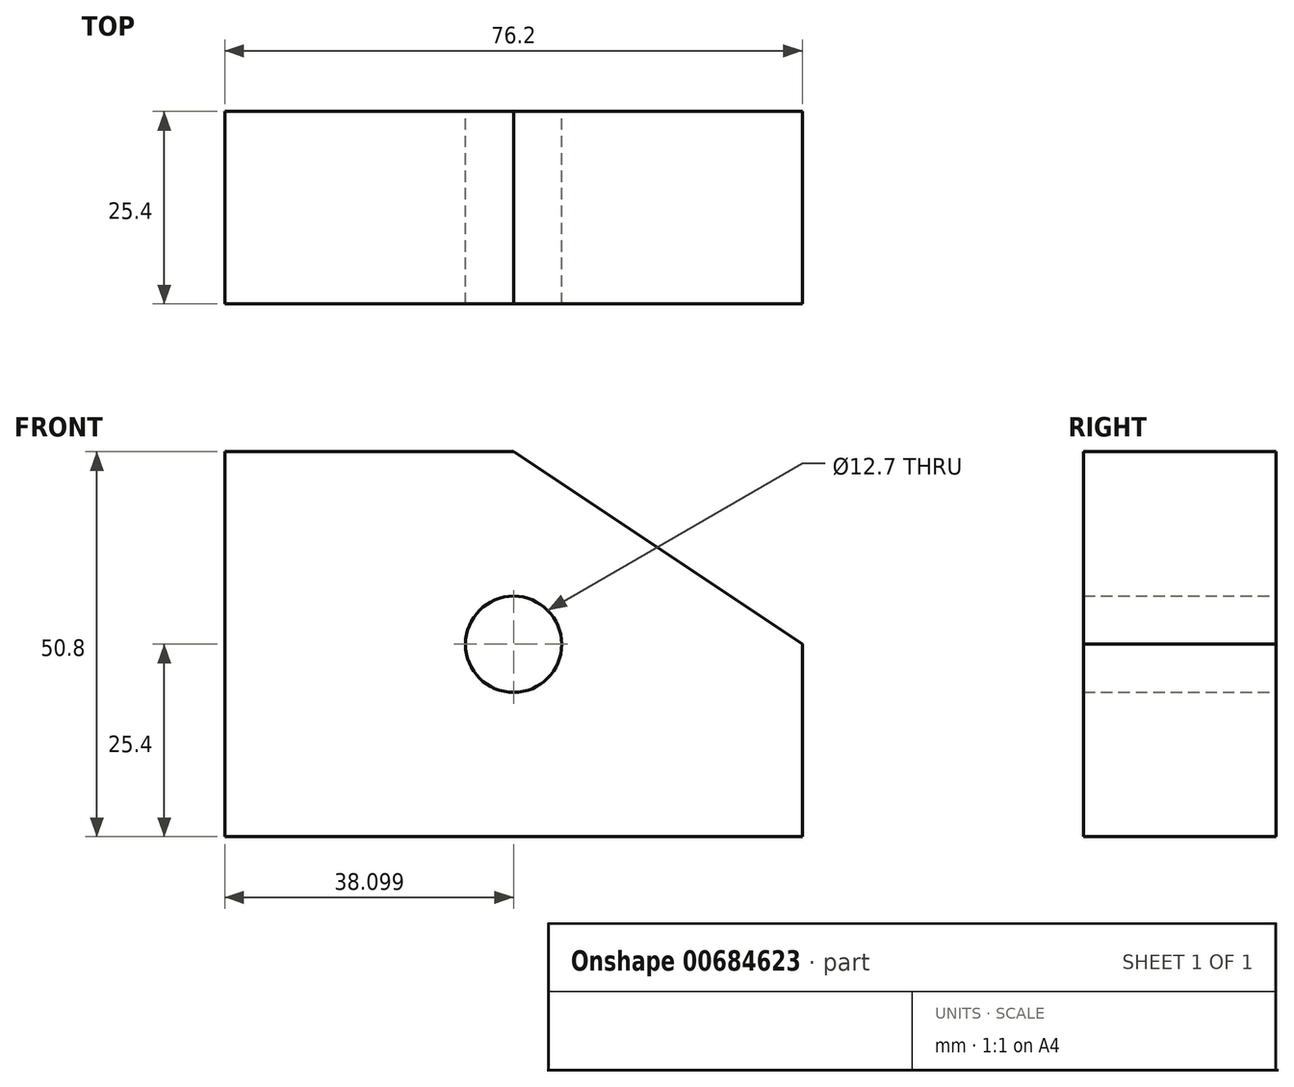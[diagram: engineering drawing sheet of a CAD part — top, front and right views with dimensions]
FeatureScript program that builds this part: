
annotation { "Feature Type Name" : "Feature", "Feature Type Description" : "" }
export const myFeature = defineFeature(function(context is Context, id is Id, definition is map)
    precondition{}
    {
        {
            var Q0;
            Q0=qCreatedBy(makeId("Front.planeOp"),FACE);
            var sketch = newSketch(context, id + "F0", { "sketchPlane" : qUnion([Q0])});
            skLineSegment(sketch, "E0", {"start": v(-42.01, 25.4) * mm, "end": v(-42.01, -25.4) * mm});
            skLineSegment(sketch, "E1", {"start": v(-42.01, -25.4) * mm, "end": v(34.19, -25.4) * mm});
            skLineSegment(sketch, "E2", {"start": v(34.19, -25.4) * mm, "end": v(34.19, 0) * mm});
            skLineSegment(sketch, "E3", {"start": v(-42.01, 25.4) * mm, "end": v(-3.91, 25.4) * mm});
            skLineSegment(sketch, "E4", {"start": v(-3.91, 25.4) * mm, "end": v(34.19, 0) * mm});
            skCircle(sketch, "E5", {"center": v(-3.91, 0) * mm, "radius": 6.35 * mm});
            skSolve(sketch);
        }
        {
            var Q0;
            Q0 = qSketchRegion(id + "F0", true);
            extrude(context, id + "F1", {"entities" : qUnion([Q0]), "depth" : 25.4 * mm, "offsetDistance" : 25.4 * mm});
        }
    });
